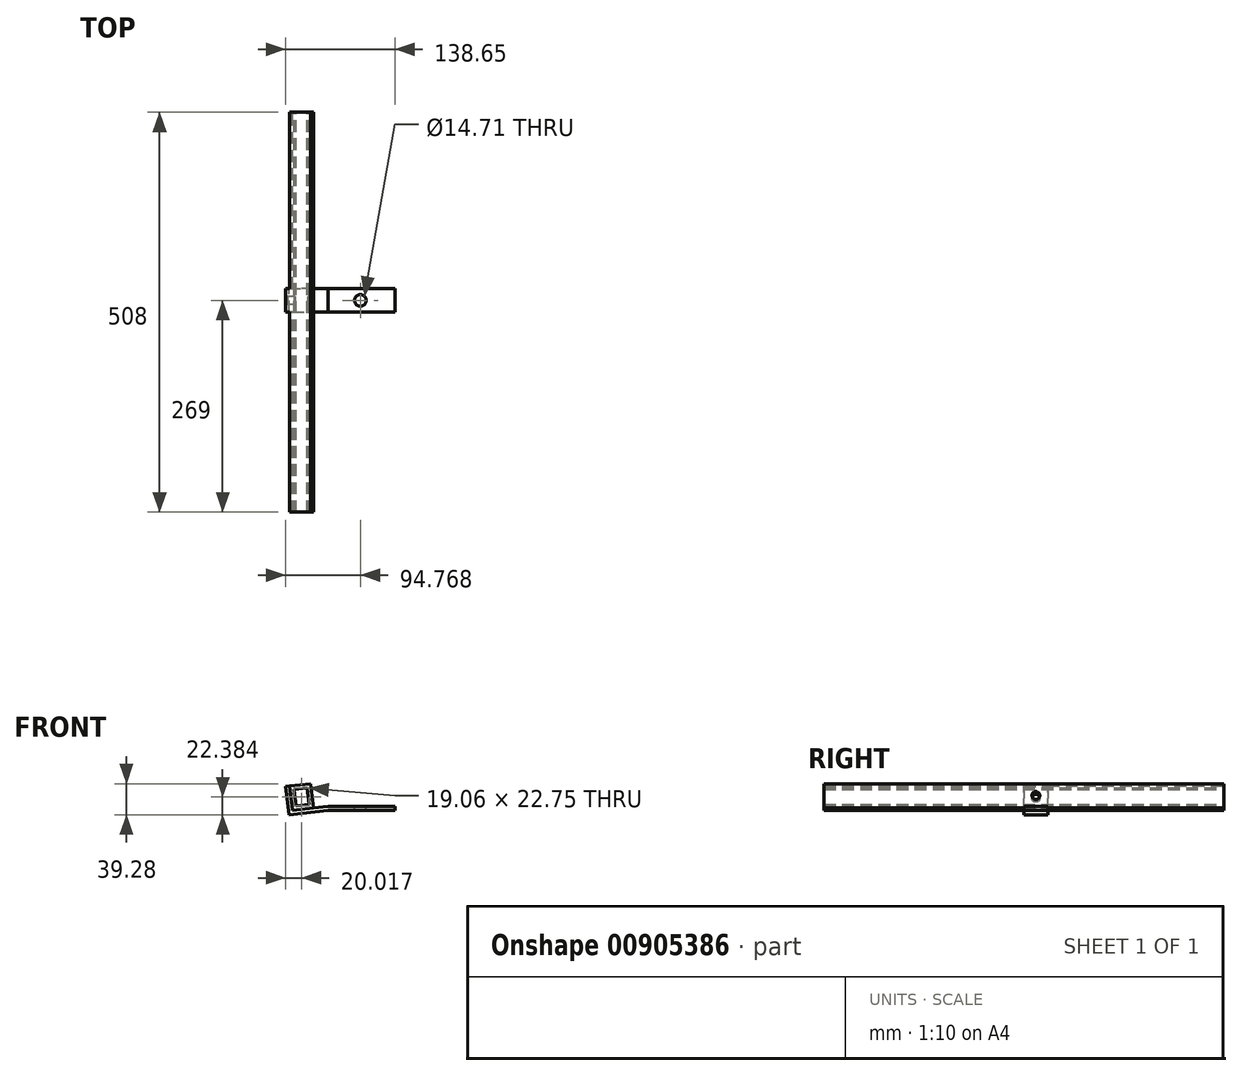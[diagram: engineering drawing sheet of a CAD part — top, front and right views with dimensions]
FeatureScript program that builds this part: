
annotation { "Feature Type Name" : "Feature", "Feature Type Description" : "" }
export const myFeature = defineFeature(function(context is Context, id is Id, definition is map)
    precondition{}
    {
        {
            var Q0;
            Q0=qCreatedBy(makeId("Front.planeOp"),FACE);
            var sketch = newSketch(context, id + "F0", { "sketchPlane" : qUnion([Q0])});
            skLineSegment(sketch, "E0", {"start": v(-3.95, 35.78) * mm, "end": v(0, 0) * mm});
            skLineSegment(sketch, "E1", {"start": v(0, 0) * mm, "end": v(49.7, 5.49) * mm});
            skLineSegment(sketch, "E2", {"start": v(49.7, 5.49) * mm, "end": v(134.7, 5.49) * mm});
            skLineSegment(sketch, "E3", {"start": v(134.7, 5.49) * mm, "end": v(134.7, 10.49) * mm});
            skLineSegment(sketch, "E4", {"start": v(134.7, 10.49) * mm, "end": v(49.7, 10.49) * mm});
            skLineSegment(sketch, "E5", {"start": v(49.7, 10.49) * mm, "end": v(4.42, 5.49) * mm});
            skLineSegment(sketch, "E6", {"start": v(4.42, 5.49) * mm, "end": v(1.02, 36.33) * mm});
            skLineSegment(sketch, "E7", {"start": v(1.02, 36.33) * mm, "end": v(-3.95, 35.78) * mm});
            skSolve(sketch);
        }
        {
            var Q0;
            Q0=makeQuery(id+"F0.imprint","IMPRINT",FACE,{"disambiguationData":[TD([[makeQuery(id+"F0.imprint","IMPRINT",EDGE,{"derivedFrom":sQuery(id+"F0.wireOp",EDGE,"E0")}),1.0]])]});
            extrude(context, id + "F1", {"entities" : qUnion([Q0]), "depth" : 30 * mm, "offsetDistance" : 25.4 * mm});
        }
        {
            var Q0;
            Q0=makeQuery(id+"F1.opExtrude","SWEPT_FACE",FACE,{"disambiguationData":[OSD([sQuery(id+"F0.wireOp",EDGE,"E4")])]});
            var sketch = newSketch(context, id + "F2", { "sketchPlane" : qUnion([Q0])});
            skCircle(sketch, "E8", {"center": v(90.82, -15) * mm, "radius": 7.36 * mm});
            skLineSegment(sketch, "E9", {"start": v(134.7, -15) * mm, "end": v(46.94, -15) * mm, "construction": true});
            skPoint(sketch, "E9.endSnap0", {"position": v(49.7, -15) * mm});
            skSolve(sketch);
        }
        {
            var Q0;
            Q0=makeQuery(id+"F2.imprint","IMPRINT",FACE,{"disambiguationData":[TD([[makeQuery(id+"F2.imprint","IMPRINT",EDGE,{"derivedFrom":sQuery(id+"F2.wireOp",EDGE,"E8")}),1.0]])]});
            extrude(context, id + "F3", {"entities" : qUnion([Q0]), "operationType" : NewBodyOperationType.REMOVE, "endBound" : BoundingType.THROUGH_ALL, "oppositeDirection" : true, "depth" : 25.4 * mm, "offsetDistance" : 25.4 * mm});
        }
        {
            var Q0;
            Q0=makeQuery(id+"F1.opExtrude","SWEPT_FACE",FACE,{"disambiguationData":[OSD([sQuery(id+"F0.wireOp",EDGE,"E0")])]});
            var sketch = newSketch(context, id + "F4", { "sketchPlane" : qUnion([Q0])});
            skLineSegment(sketch, "E10", {"start": v(15, 36) * mm, "end": v(15, 0) * mm, "construction": true});
            skCircle(sketch, "E11", {"center": v(15, 21) * mm, "radius": 4.96 * mm});
            skSolve(sketch);
        }
        {
            var Q0;
            Q0=makeQuery(id+"F4.imprint","IMPRINT",FACE,{"disambiguationData":[TD([[makeQuery(id+"F4.imprint","IMPRINT",EDGE,{"derivedFrom":sQuery(id+"F4.wireOp",EDGE,"E11")}),1.0]])]});
            extrude(context, id + "F5", {"entities" : qUnion([Q0]), "operationType" : NewBodyOperationType.REMOVE, "endBound" : BoundingType.THROUGH_ALL, "oppositeDirection" : true, "depth" : 25.4 * mm, "offsetDistance" : 25.4 * mm});
        }
        {
            var Q0;
            Q0=makeQuery(id+"F1.opExtrude","CAP_FACE",FACE,{"disambiguationData":[OSD([sQuery(id+"F0.wireOp",EDGE,"E0"),sQuery(id+"F0.wireOp",EDGE,"E1"),sQuery(id+"F0.wireOp",EDGE,"E2"),sQuery(id+"F0.wireOp",EDGE,"E3"),sQuery(id+"F0.wireOp",EDGE,"E4"),sQuery(id+"F0.wireOp",EDGE,"E5"),sQuery(id+"F0.wireOp",EDGE,"E6"),sQuery(id+"F0.wireOp",EDGE,"E7")])],"isStart":false});
            var sketch = newSketch(context, id + "F6", { "sketchPlane" : qUnion([Q0])});
            skLineSegment(sketch, "E12", {"start": v(1.02, 36.33) * mm, "end": v(27.71, 39.28) * mm});
            skLineSegment(sketch, "E13", {"start": v(27.71, 39.28) * mm, "end": v(31.12, 8.44) * mm});
            skLineSegment(sketch, "E14", {"start": v(6.54, 31.91) * mm, "end": v(23.29, 33.76) * mm});
            skLineSegment(sketch, "E15", {"start": v(23.29, 33.76) * mm, "end": v(25.6, 12.86) * mm});
            skLineSegment(sketch, "E16", {"start": v(25.6, 12.86) * mm, "end": v(8.85, 11) * mm});
            skLineSegment(sketch, "E17", {"start": v(8.85, 11) * mm, "end": v(6.54, 31.91) * mm});
            skSolve(sketch);
        }
        {
            var Q0;
            Q0=makeQuery(id+"F6.imprint","IMPRINT",FACE,{"disambiguationData":[TD([[makeQuery(id+"F6.imprint","IMPRINT",EDGE,{"derivedFrom":sQuery(id+"F6.wireOp",EDGE,"E12")}),-1.0]])]});
            extrude(context, id + "F7", {"entities" : qUnion([Q0]), "operationType" : NewBodyOperationType.ADD, "endBound" : BoundingType.SYMMETRIC, "depth" : 508 * mm, "offsetDistance" : 25.4 * mm});
        }
        {
            var Q0;
            Q0=makeQuery(id+"F7.boolean.opBoolean","SPLIT",FACE,{"disambiguationData":[TD([makeQuery(id+"F5.boolean.opBoolean","COPY",FACE,{"derivedFrom":makeQuery(id+"F5.opExtrude","SWEPT_FACE",FACE,{"disambiguationData":[OSD([sQuery(id+"F4.wireOp",EDGE,"E11")])]})})])],"derivedFrom":makeQuery(id+"F7.opExtrude","SWEPT_FACE",FACE,{"disambiguationData":[OSD([sQuery(id+"F0.wireOp",EDGE,"E6")])]})});
            extrude(context, id + "F8", {"entities" : qUnion([Q0]), "operationType" : NewBodyOperationType.REMOVE, "endBound" : BoundingType.THROUGH_ALL, "oppositeDirection" : true, "depth" : 25.4 * mm, "offsetDistance" : 25.4 * mm});
        }
    });
